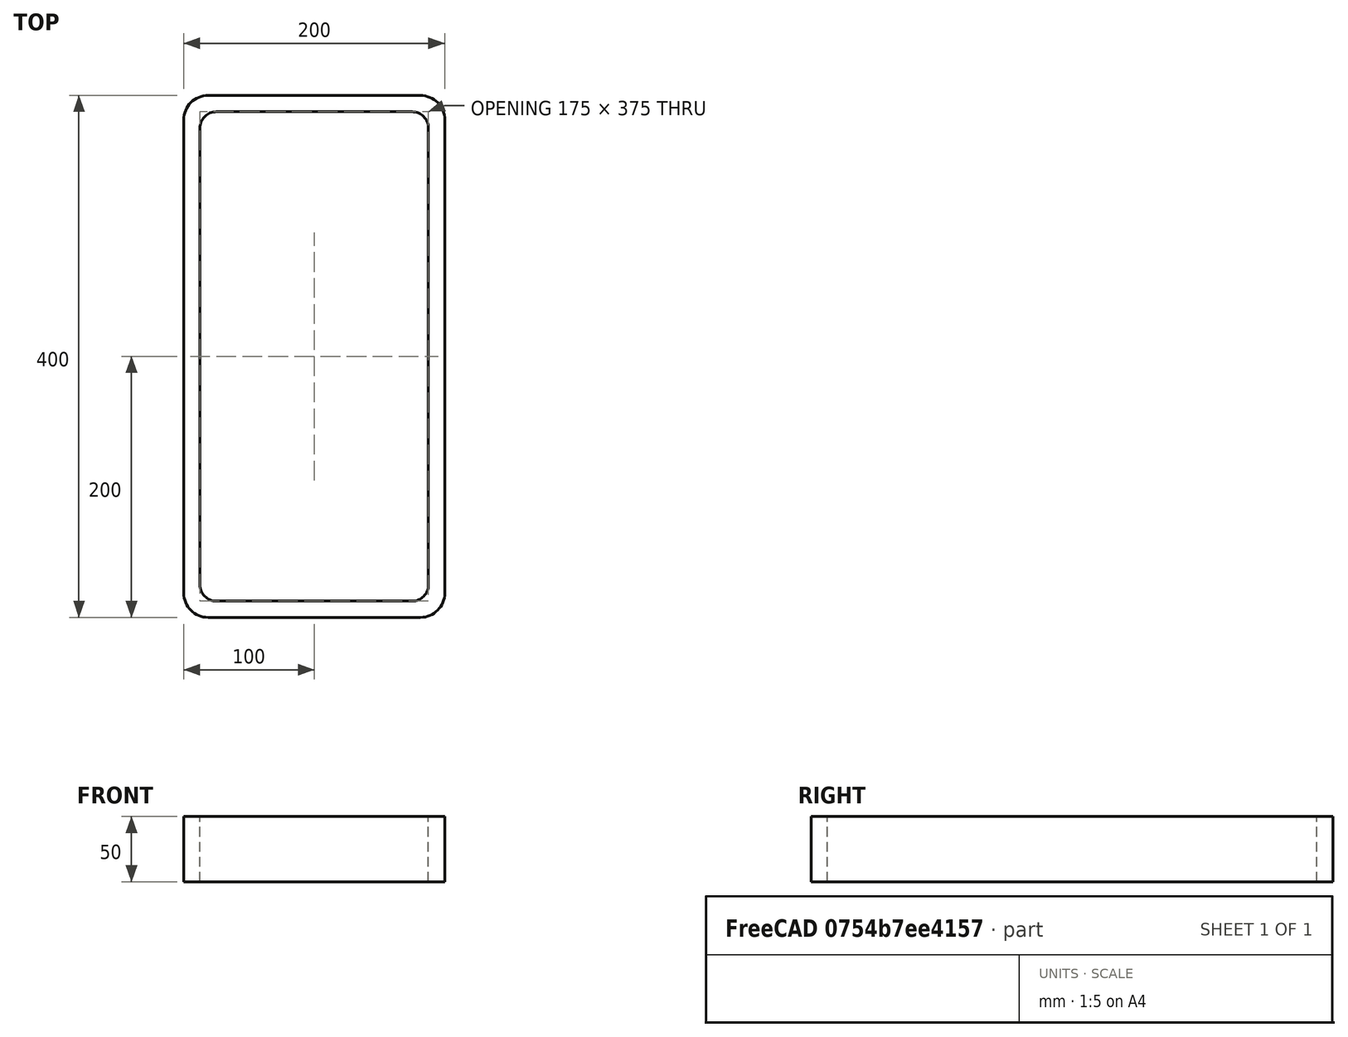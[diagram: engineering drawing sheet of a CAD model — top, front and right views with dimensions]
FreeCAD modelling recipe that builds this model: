
FCSTD DOCUMENT  (FreeCAD 0.15R4671 (Git))
Label: Rectangular hollow section 400x200x12.5 EN10219 S235JRH
License: All rights reserved
LicenseURL: http://en.wikipedia.org/wiki/All_rights_reserved
objects: Sketcher::SketchObject×1, Part::Extrusion×1
note: 2 computed .brp shape members not serialized (recipe doc carries the construction recipe); baked Part::Feature solids carry a one-line shape summary decoded from their .brp

FEATURE [Sketcher::SketchObject] Sketch
  sketch-geometry (16):
    g0: LineSegment StartX=-75 StartY=187.5 StartZ=0 EndX=75 EndY=187.5 EndZ=0
    g1: LineSegment StartX=87.5 StartY=175 StartZ=0 EndX=87.5 EndY=-175 EndZ=0
    g2: LineSegment StartX=75 StartY=-187.5 StartZ=0 EndX=-75 EndY=-187.5 EndZ=0
    g3: LineSegment StartX=-87.5 StartY=-175 StartZ=0 EndX=-87.5 EndY=175 EndZ=0
    g4: LineSegment StartX=-81.25 StartY=200 StartZ=0 EndX=81.25 EndY=200 EndZ=0
    g5: LineSegment StartX=100 StartY=181.25 StartZ=0 EndX=100 EndY=-181.25 EndZ=0
    g6: LineSegment StartX=81.25 StartY=-200 StartZ=0 EndX=-81.25 EndY=-200 EndZ=0
    g7: LineSegment StartX=-100 StartY=-181.25 StartZ=0 EndX=-100 EndY=181.25 EndZ=0
    g8: ArcOfCircle CenterX=-75 CenterY=175 CenterZ=0 NormalX=0 NormalY=0 NormalZ=1 Radius=12.5 StartAngle=1.5708 EndAngle=3.14159
    g9: ArcOfCircle CenterX=75 CenterY=175 CenterZ=0 NormalX=0 NormalY=0 NormalZ=1 Radius=12.5 StartAngle=0 EndAngle=1.5708
    g10: ArcOfCircle CenterX=75 CenterY=-175 CenterZ=0 NormalX=0 NormalY=0 NormalZ=1 Radius=12.5 StartAngle=4.71239 EndAngle=6.28319
    g11: ArcOfCircle CenterX=-75 CenterY=-175 CenterZ=0 NormalX=0 NormalY=0 NormalZ=1 Radius=12.5 StartAngle=3.14159 EndAngle=4.71239
    g12: ArcOfCircle CenterX=81.25 CenterY=181.25 CenterZ=0 NormalX=0 NormalY=0 NormalZ=1 Radius=18.75 StartAngle=0 EndAngle=1.5708
    g13: ArcOfCircle CenterX=81.25 CenterY=-181.25 CenterZ=0 NormalX=0 NormalY=0 NormalZ=1 Radius=18.75 StartAngle=4.71239 EndAngle=6.28319
    g14: ArcOfCircle CenterX=-81.25 CenterY=-181.25 CenterZ=0 NormalX=0 NormalY=0 NormalZ=1 Radius=18.75 StartAngle=3.14159 EndAngle=4.71239
    g15: ArcOfCircle CenterX=-81.25 CenterY=181.25 CenterZ=0 NormalX=0 NormalY=0 NormalZ=1 Radius=18.75 StartAngle=1.5708 EndAngle=3.14159
  constraints (36):
    c: Horizontal(g2)
    c: Vertical(g3)
    c: Horizontal(g6)
    c: Vertical(g7)
    c: Tangent(g3,g8) = 1.5708
    c: Tangent(g0,g8) = 1.5708
    c: Tangent(g0,g9) = 1.5708
    c: Tangent(g1,g9) = 1.5708
    c: Tangent(g1,g10) = 1.5708
    c: Tangent(g2,g10) = 1.5708
    c: Tangent(g2,g11) = 1.5708
    c: Tangent(g3,g11) = 1.5708
    c: Tangent(g4,g12) = 1.5708
    c: Tangent(g5,g12) = 1.5708
    c: Tangent(g5,g13) = 1.5708
    c: Tangent(g6,g13) = 1.5708
    c: Tangent(g6,g14) = 1.5708
    c: Tangent(g7,g14) = 1.5708
    c: Tangent(g7,g15) = 1.5708
    c: Tangent(g4,g15) = 1.5708
    c: Equal(g9,g8)
    c: Equal(g9,g11)
    c: Equal(g9,g10)
    c: Equal(g12,g15)
    c: Equal(g12,g14)
    c: Equal(g12,g13)
    c: Symmetric(g4,g6,g-1)
    c: Symmetric(g7,g5,g-2)
    c: DistanceY(g4,g6) = -400
    c: DistanceX(g7,g5) = 200
    c: Symmetric(g3,g1,g-2)
    c: Symmetric(g0,g2,g-1)
    c: DistanceY(g0,g4) = 12.5
    c: DistanceX(g5,g1) = -12.5
    c: Radius(g9) = 12.5
    c: Radius(g12) = 18.75
FEATURE [Part::Extrusion] Extrude  label="Rectangular hollow section 400x200x12.5 EN10219 S235JRH"
  Base = -> Sketch
  Dir = (0,0,50)
  Solid = true
